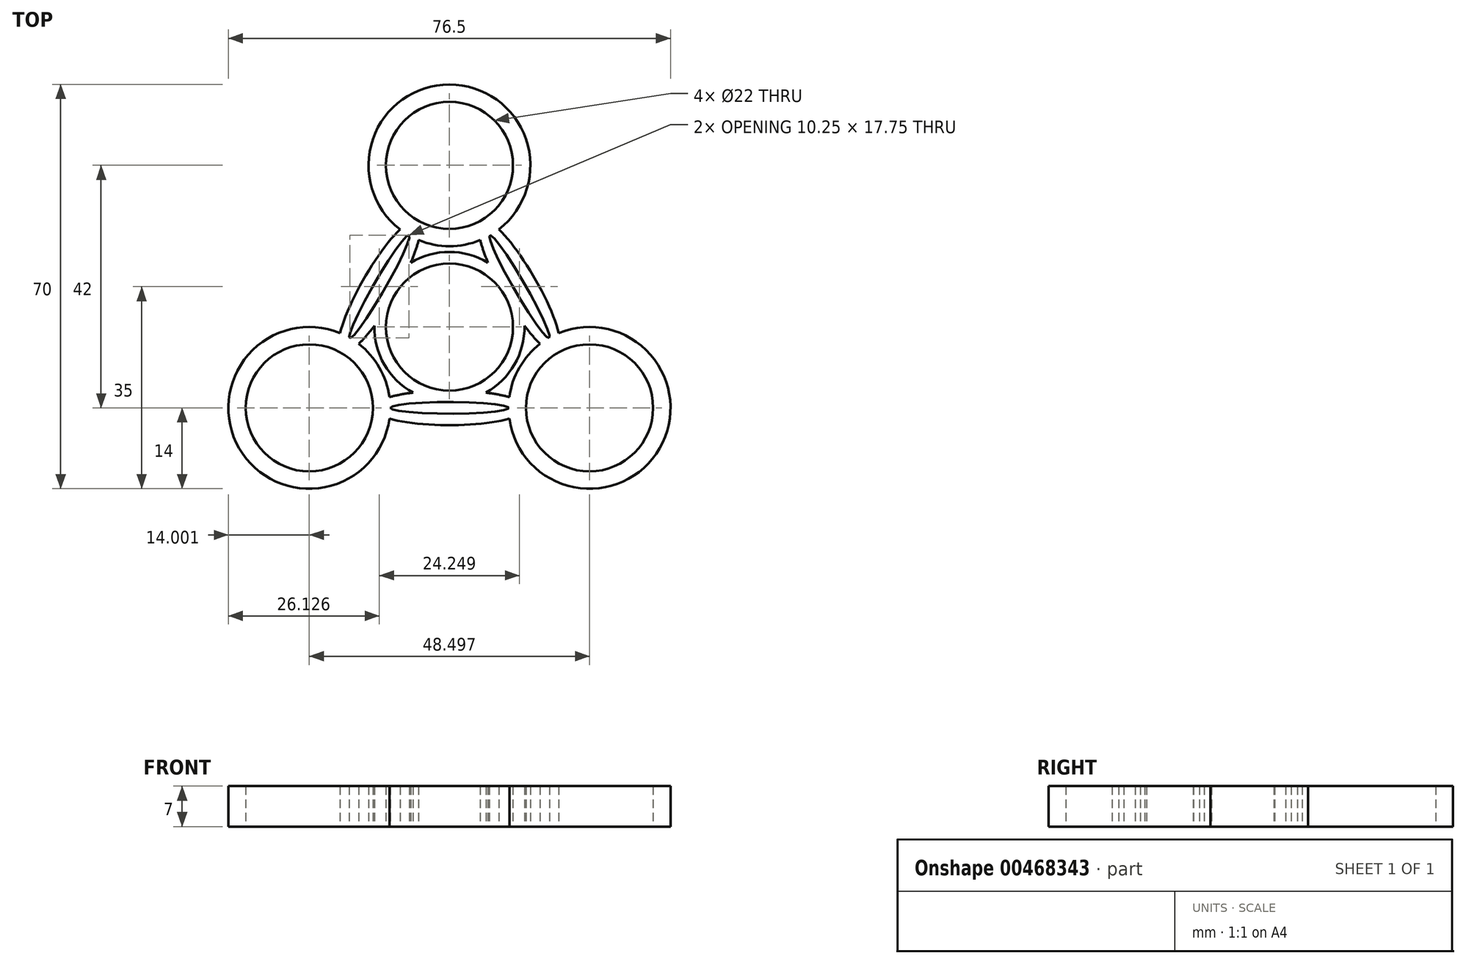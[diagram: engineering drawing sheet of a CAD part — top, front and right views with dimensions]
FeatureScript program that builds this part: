
annotation { "Feature Type Name" : "Feature", "Feature Type Description" : "" }
export const myFeature = defineFeature(function(context is Context, id is Id, definition is map)
    precondition{}
    {
        {
            var Q0;
            Q0=qCreatedBy(makeId("Top.planeOp"),FACE);
            var sketch = newSketch(context, id + "F0", { "sketchPlane" : qUnion([Q0])});
            skCircle(sketch, "E0", {"center": v(0, 0) * mm, "radius": 11 * mm});
            skCircle(sketch, "E1", {"center": v(0, 28) * mm, "radius": 11 * mm});
            skCircle(sketch, "E2.0", {"center": v(0, 28) * mm, "radius": 14 * mm});
            skArc(sketch, "E3.0", {"start": v(6.68, 11.15) * mm, "mid": v(-11.26, -6.5) * mm, "end": v(13, 0.21) * mm});
            skCircle(sketch, "E4.1.0", {"center": v(-24.25, -14) * mm, "radius": 14 * mm});
            skCircle(sketch, "E4.1.1", {"center": v(-24.25, -14) * mm, "radius": 11 * mm});
            skCircle(sketch, "E4.2.0", {"center": v(24.25, -14) * mm, "radius": 14 * mm});
            skCircle(sketch, "E4.2.1", {"center": v(24.25, -14) * mm, "radius": 11 * mm});
            skLineSegment(sketch, "E5", {"start": v(24.25, -14) * mm, "end": v(17.25, -1.88) * mm});
            skPoint(sketch, "E6", {"position": v(12.12, 7) * mm});
            skPoint(sketch, "E7", {"position": v(5.5, 18.47) * mm});
            skPoint(sketch, "E8", {"position": v(7, 15.88) * mm});
            skPoint(sketch, "E9", {"position": v(9.53, 5.5) * mm});
            skPoint(sketch, "E10", {"position": v(11.26, 6.5) * mm});
            skEllipse(sketch, "E11", {"center": v(12.12, 7) * mm, "majorRadius": 1 * mm, "minorRadius": 10.25 * mm, "majorAxis": v(-0.87, -0.5)});
            skEllipticalArc(sketch, "E12", {});
            skLineSegment(sketch, "E13.trimOffspring", {"start": v(5.5, 18.47) * mm, "end": v(0, 28) * mm});
            skEllipticalArc(sketch, "E14.1.0", {});
            skEllipse(sketch, "E14.1.1", {"center": v(-12.12, 7) * mm, "majorRadius": 1 * mm, "minorRadius": 10.25 * mm, "majorAxis": v(0.87, -0.5)});
            skEllipticalArc(sketch, "E14.2.0", {});
            skEllipse(sketch, "E14.2.1", {"center": v(0, -14) * mm, "majorRadius": 1 * mm, "minorRadius": 10.25 * mm, "majorAxis": v(0, 1)});
            skEllipticalArc(sketch, "E15.trimOffspring", {});
            skEllipticalArc(sketch, "E16.trimOffspring", {});
            skEllipticalArc(sketch, "E17.trimOffspring", {});
            skEllipticalArc(sketch, "E18.trimOffspring", {});
            skEllipticalArc(sketch, "E19.trimOffspring", {});
            skEllipticalArc(sketch, "E20.trimOffspring", {});
            const initialGuessF0  = {"E12": [0.012124355652982135, 0.007, -0.8660254037844389, -0.5, 0.003, 0.013248711305964282, 5.383723669402354, 6.283185307179586], "E14.1.0": [-0.01212435565298213, 0.007, 0.8660254037844383, -0.5, 0.003, 0.013248711305964282, 0.4968922354947489, 0.8994616377772289], "E14.2.0": [0, -0.014, 0, 1, 0.003, 0.013248711305964282, 5.383723669402354, 5.78629307168483], "E15.trimOffspring": [0.012124355652982135, 0.007, -0.8660254037844389, -0.5, 0.003, 0.013248711305964282, 2.2421310158125616, 4.0410542913670255], "E16.trimOffspring": [0.012124355652982135, 0.007, -0.8660254037844389, -0.5, 0.003, 0.013248711305964282, 0.4968922354947516, 0.8994616377772324], "E17.trimOffspring": [0, -0.014, 0, 1, 0.003, 0.013248711305964282, 0.4968922354947498, 0.8994616377772324], "E18.trimOffspring": [0, -0.014, 0, 1, 0.003, 0.013248711305964282, 2.2421310158125616, 4.041054291367027], "E19.trimOffspring": [-0.01212435565298213, 0.007, 0.8660254037844383, -0.5, 0.003, 0.013248711305964282, 2.2421310158125642, 4.0410542913670255], "E20.trimOffspring": [-0.01212435565298213, 0.007, 0.8660254037844383, -0.5, 0.003, 0.013248711305964282, 5.383723669402354, 5.786293071684838]};
            skSetInitialGuess(sketch, initialGuessF0);
            skSolve(sketch);
        }
        {
            var Q0;
            Q0=makeQuery(id+"F0.imprint","IMPRINT",FACE,{"disambiguationData":[TD([[makeQuery(id+"F0.imprint","IMPRINT",EDGE,{"derivedFrom":sQuery(id+"F0.wireOp",EDGE,"E1")}),-1.0]])]});
            var Q1;
            {var subQ0=sQuery(id+"F0.wireOp",EDGE,"E19.trimOffspring");Q1=makeQuery(id+"F0.imprint","IMPRINT",FACE,{"disambiguationData":[TD([[makeQuery(id+"F0.imprint","IMPRINT",EDGE,{"derivedFrom":subQ0}),1.0]])]});}
            var Q2;
            {var subQ0=sQuery(id+"F0.wireOp",EDGE,"E14.1.0");Q2=makeQuery(id+"F0.imprint","IMPRINT",FACE,{"disambiguationData":[TD([[makeQuery(id+"F0.imprint","IMPRINT",EDGE,{"derivedFrom":subQ0}),1.0]])]});}
            var Q3;
            {var subQ0=sQuery(id+"F0.wireOp",EDGE,"E20.trimOffspring");Q3=makeQuery(id+"F0.imprint","IMPRINT",FACE,{"disambiguationData":[TD([[makeQuery(id+"F0.imprint","IMPRINT",EDGE,{"derivedFrom":subQ0}),1.0]])]});}
            var Q4;
            Q4=makeQuery(id+"F0.imprint","IMPRINT",FACE,{"disambiguationData":[TD([[makeQuery(id+"F0.imprint","IMPRINT",EDGE,{"derivedFrom":sQuery(id+"F0.wireOp",EDGE,"E0")}),-1.0]])]});
            var Q5;
            {var subQ0=sQuery(id+"F0.wireOp",EDGE,"E15.trimOffspring");Q5=makeQuery(id+"F0.imprint","IMPRINT",FACE,{"disambiguationData":[TD([[makeQuery(id+"F0.imprint","IMPRINT",EDGE,{"derivedFrom":subQ0}),1.0]])]});}
            var Q6;
            Q6=makeQuery(id+"F0.imprint","IMPRINT",FACE,{"disambiguationData":[TD([[makeQuery(id+"F0.imprint","IMPRINT",EDGE,{"derivedFrom":sQuery(id+"F0.wireOp",EDGE,"E4.2.1")}),-1.0]])]});
            var Q7;
            {var subQ0=sQuery(id+"F0.wireOp",EDGE,"E18.trimOffspring");Q7=makeQuery(id+"F0.imprint","IMPRINT",FACE,{"disambiguationData":[TD([[makeQuery(id+"F0.imprint","IMPRINT",EDGE,{"derivedFrom":subQ0}),1.0]])]});}
            var Q8;
            {var subQ0=sQuery(id+"F0.wireOp",EDGE,"E14.2.0");Q8=makeQuery(id+"F0.imprint","IMPRINT",FACE,{"disambiguationData":[TD([[makeQuery(id+"F0.imprint","IMPRINT",EDGE,{"derivedFrom":subQ0}),1.0]])]});}
            var Q9;
            {var subQ0=sQuery(id+"F0.wireOp",EDGE,"E17.trimOffspring");Q9=makeQuery(id+"F0.imprint","IMPRINT",FACE,{"disambiguationData":[TD([[makeQuery(id+"F0.imprint","IMPRINT",EDGE,{"derivedFrom":subQ0}),1.0]])]});}
            var Q10;
            Q10=makeQuery(id+"F0.imprint","IMPRINT",FACE,{"disambiguationData":[TD([[makeQuery(id+"F0.imprint","IMPRINT",EDGE,{"derivedFrom":sQuery(id+"F0.wireOp",EDGE,"E4.1.1")}),-1.0]])]});
            extrude(context, id + "F1", {"entities" : qUnion([Q0, Q1, Q2, Q3, Q4, Q5, Q6, Q7, Q8, Q9, Q10]), "endBound" : BoundingType.SYMMETRIC, "depth" : 7 * mm});
        }
    });
